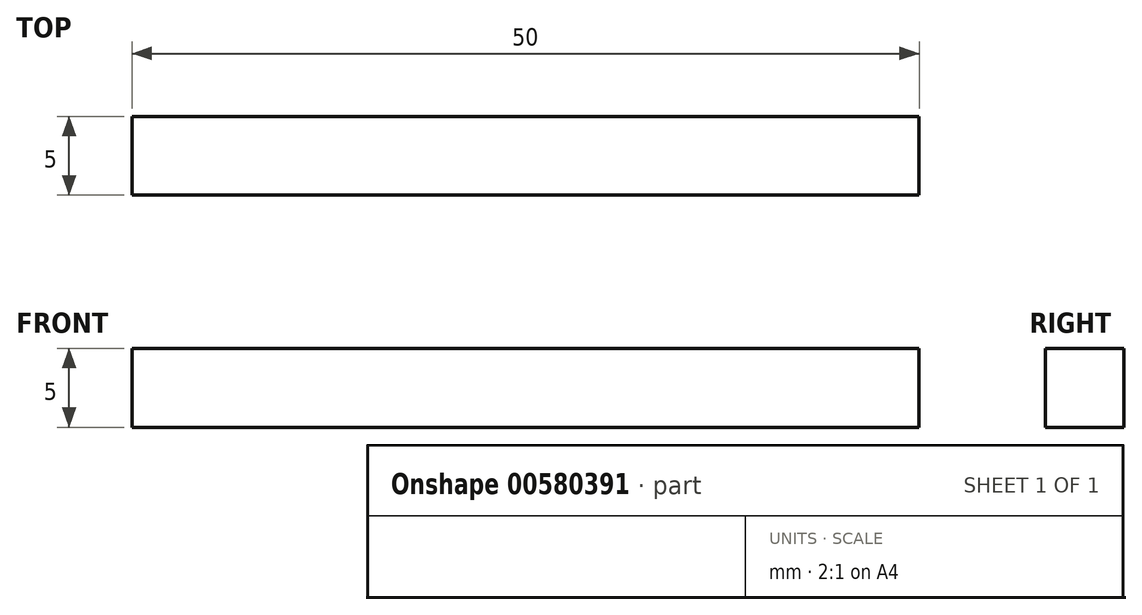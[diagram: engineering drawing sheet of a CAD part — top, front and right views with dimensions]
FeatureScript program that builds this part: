
annotation { "Feature Type Name" : "Feature", "Feature Type Description" : "" }
export const myFeature = defineFeature(function(context is Context, id is Id, definition is map)
    precondition{}
    {
        {
            var Q0;
            Q0=qCreatedBy(makeId("Front.planeOp"),FACE);
            var sketch = newSketch(context, id + "F0", { "sketchPlane" : qUnion([Q0])});
            skLineSegment(sketch, "E0", {"start": v(-7.56, 0) * mm, "end": v(-7.56, 5) * mm});
            skLineSegment(sketch, "E1", {"start": v(-7.56, 5) * mm, "end": v(42.44, 5) * mm});
            skLineSegment(sketch, "E2", {"start": v(42.44, 5) * mm, "end": v(42.44, 0) * mm});
            skLineSegment(sketch, "E3", {"start": v(42.44, 0) * mm, "end": v(-7.56, 0) * mm});
            skSolve(sketch);
        }
        {
            var Q0;
            Q0 = qSketchRegion(id + "F0", true);
            extrude(context, id + "F1", {"entities" : qUnion([Q0]), "depth" : 5 * mm, "offsetDistance" : 25 * mm});
        }
        {
            var Q0;
            Q0=qCreatedBy(makeId("Front.planeOp"),FACE);
            var sketch = newSketch(context, id + "F2", { "sketchPlane" : qUnion([Q0])});
            skLineSegment(sketch, "E4", {"start": v(-60.8, 0) * mm, "end": v(-60.8, 50) * mm});
            skLineSegment(sketch, "E5", {"start": v(-60.8, 50) * mm, "end": v(-55.8, 50) * mm});
            skLineSegment(sketch, "E6", {"start": v(-55.8, 50) * mm, "end": v(-55.8, 0) * mm});
            skLineSegment(sketch, "E7", {"start": v(-55.8, 0) * mm, "end": v(-60.8, 0) * mm});
            skSolve(sketch);
        }
        {
            var Q0;
            Q0=makeQuery(id+"F2.imprint","IMPRINT",FACE,{"disambiguationData":[TD([[makeQuery(id+"F2.imprint","IMPRINT",EDGE,{"derivedFrom":sQuery(id+"F2.wireOp",EDGE,"E4")}),-1.0]])]});
            extrude(context, id + "F3", {"entities" : qUnion([Q0]), "depth" : 5 * mm, "offsetDistance" : 25 * mm});
        }
        {
            var Q0;
            Q0=makeQuery(id+"F3.opExtrude","SWEPT_BODY",BODY,{"disambiguationData":[OSD([sQuery(id+"F2.wireOp",EDGE,"E4"),sQuery(id+"F2.wireOp",EDGE,"E5"),sQuery(id+"F2.wireOp",EDGE,"E6"),sQuery(id+"F2.wireOp",EDGE,"E7")])]});
            deleteBodies(context, id + "F4", {"entities" : qUnion([Q0])});
        }
    });
